# Revit family: A35_4
name_source: partatom
category: Structural Connections
revit_build: Autodesk Revit 2014 (Build: 20130308_1515(x64)
units: mm (PartAtom-declared; Revit-internal decimal feet)

## types (1)
- A35_4
    A = 34 mm
    B = 114 mm  [stored 0.374016 ft]
    C = 34 mm
    Date Last Modified = September 09, 2016
    Default Elevation = 0 mm  [stored 0 ft]
    Description = Framing Anchor
    E = 39 mm  [stored 0.127953 ft]
    Family Version = 1.0.0
    Manufacturer = Simpson Strong-Tie Company Inc.
    Model = A35/4
    Model Disclaimer = Contact Simpson Strong-Tie Company Inc. for more information
    Product Type = Framing Anchor
    Provide Feedback = http://www.strongtie.com
    URL = www.strongtie.eu\s\A35
    t = 1 mm  [stored 0.00328084 ft]

note: [stored X ft] marks values corroborated as IEEE doubles in the binary element streams (Revit-internal decimal feet)

## geometry (parser evidence)
native form markers: Blend x77, Sweep x1
no freeform markers — native parametric forms only
